# Revit family: Reece_Basin_American Standard_Heron_Above Counter Basin_Square_Vessel_499 mm
name_source: partatom
category: Plumbing Fixtures
revit_build: Autodesk Revit 2018 (Build: 20190510_1515(x64)
units: mm (PartAtom-declared; Revit-internal decimal feet)

## family parameters
Cut with Voids When Loaded = No
Host = Face
Part Type = Normal
Room Calculation Point = Yes
Round Connector Dimension = Use Diameter
Shared = Yes

## types (1)
- No Taphole_Fine Fire Clay Ceramic_White
    CWFU = 0
    Default Elevation = 1000 mm  [stored 3.28084 ft]
    Description = American Standard Heron Square Vessel Basin No Taphole White
    Disclaimer = THIS FILE IS THE PROPERTY OF THE REECE GROUP. IT MAY NOT BE REPRODUCED, REVERSE-ENGINEERED OR MODIFIED. ANY REPUBLICATION, TRANSMISSION OR DISTRIBUTION FOR THE PURPOSE OF COMMERCIALLY EXPLOITING THE FILES IS PROHIBITED.
    HWFU = 0
    Keynote = Product #9506428, Reece_Basin_American Standard_Heron_Above Counter Basin_Square_Vessel_499 mm - No Taphole_Fine Fire Clay Ceramic_White
    Manufacturer = American Standard
    Model = Heron
    Reece_Basin_Outlet = 40 mm  [stored 0.131234 ft]
    Reece_Detail_Additional = Square
    Reece_Detail_Connector = No Taphole
    Reece_Detail_Disclaimer = THIS FILE IS THE PROPERTY OF THE REECE GROUP. IT MAY NOT BE REPRODUCED, REVERSE-ENGINEERED OR MODIFIED. ANY REPUBLICATION, TRANSMISSION OR DISTRIBUTION FOR THE PURPOSE OF COMMERCIALLY EXPLOITING THE FILES IS PROHIBITED.
    Reece_Detail_Installation = Above Counter Basin
    Reece_Material-Main = Reece_Ceramic_Fine Fire Clay_White
    Reece_Material_Secondary = Reece_Brass_Chrome
    Reece_Overall_Capacity = 21 L
    Reece_Overall_Height = 150 mm
    Reece_Overall_Length = 399 mm  [stored 1.30906 ft]
    Reece_Overall_Width = 499 mm  [stored 1.63714 ft]
    Reece_Product_Brand = American Standard
    Reece_Product_Description = American Standard Heron Square Vessel Basin No Taphole White
    Reece_Product_Mount = Above Counter
    Reece_Product_Number = 9506428
    Reece_Product_Sub Brand = Heron
    Reece_Product_Type = Basin
    Reece_Product_Web Page = https://www.reece.com.au
    Type Comments = Basin
    URL = https://www.reece.com.au
    WFU = 0

note: [stored X ft] marks values corroborated as IEEE doubles in the binary element streams (Revit-internal decimal feet)

## geometry (parser evidence)
native form markers: Sweep x2
no freeform markers — native parametric forms only
